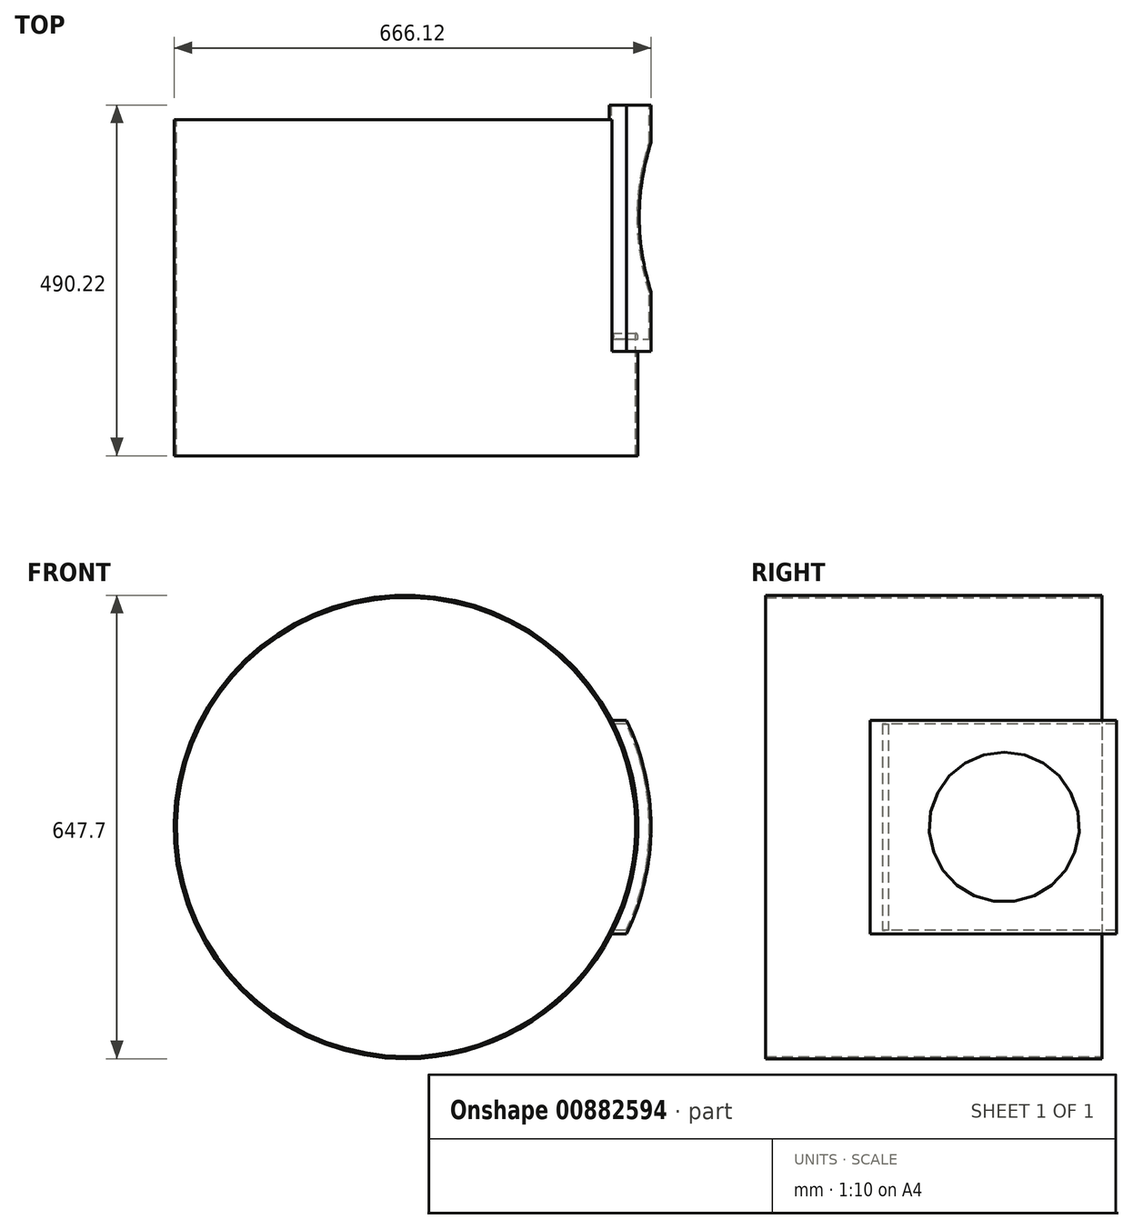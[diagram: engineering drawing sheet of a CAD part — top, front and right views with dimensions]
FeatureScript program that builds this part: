
annotation { "Feature Type Name" : "Feature", "Feature Type Description" : "" }
export const myFeature = defineFeature(function(context is Context, id is Id, definition is map)
    precondition{}
    {
        {
            var Q0;
            Q0=qCreatedBy(makeId("Front.planeOp"),FACE);
            var sketch = newSketch(context, id + "F0", { "sketchPlane" : qUnion([Q0])});
            skCircle(sketch, "E0", {"center": v(0, 0) * mm, "radius": 320.68 * mm});
            skCircle(sketch, "E1", {"center": v(0, 0) * mm, "radius": 323.85 * mm});
            skSolve(sketch);
        }
        {
            var Q0;
            Q0 = qSketchRegion(id + "F0", true);
            extrude(context, id + "F1", {"entities" : qUnion([Q0]), "depth" : 469.9 * mm, "offsetDistance" : 25.4 * mm});
        }
        {
            var Q0;
            Q0=qCreatedBy(makeId("Right.planeOp"),FACE);
            var sketch = newSketch(context, id + "F2", { "sketchPlane" : qUnion([Q0])});
            skLineSegment(sketch, "E2", {"start": v(0, 0) * mm, "end": v(-469.9, 0) * mm, "construction": true});
            skLineSegment(sketch, "E3.bottom", {"start": v(0, 149.23) * mm, "end": v(-298.45, 149.23) * mm});
            skLineSegment(sketch, "E3.top", {"start": v(0, -149.22) * mm, "end": v(-298.45, -149.22) * mm});
            skLineSegment(sketch, "E3.left", {"start": v(0, 149.22) * mm, "end": v(0, -149.23) * mm});
            skLineSegment(sketch, "E3.right", {"start": v(-298.45, 149.23) * mm, "end": v(-298.45, -149.22) * mm});
            skPoint(sketch, "E3.middle", {"position": v(-149.23, 0) * mm});
            skSolve(sketch);
        }
        {
            var Q0;
            Q0 = qSketchRegion(id + "F2", true);
            extrude(context, id + "F3", {"entities" : qUnion([Q0]), "operationType" : NewBodyOperationType.REMOVE, "depth" : 595.88 * mm, "offsetDistance" : 25.4 * mm});
        }
        {
            var Q0;
            Q0=qCreatedBy(makeId("Right.planeOp"),FACE);
            var sketch = newSketch(context, id + "F4", { "sketchPlane" : qUnion([Q0])});
            skLineSegment(sketch, "E4", {"start": v(0, 0) * mm, "end": v(-447.9, 0) * mm, "construction": true});
            skPoint(sketch, "E5", {"position": v(-161.92, 0) * mm});
            skLineSegment(sketch, "E6.bottom", {"start": v(0, 149.23) * mm, "end": v(-323.85, 149.22) * mm});
            skLineSegment(sketch, "E6.top", {"start": v(0, -149.22) * mm, "end": v(-323.85, -149.23) * mm});
            skLineSegment(sketch, "E6.right", {"start": v(-323.85, 149.22) * mm, "end": v(-323.85, -149.23) * mm});
            skLineSegment(sketch, "E7.bottom", {"start": v(-17.14, 144.15) * mm, "end": v(-306.71, 144.15) * mm});
            skLineSegment(sketch, "E7.top", {"start": v(-17.14, -144.15) * mm, "end": v(-306.71, -144.15) * mm});
            skLineSegment(sketch, "E7.right", {"start": v(-306.71, 144.15) * mm, "end": v(-306.71, -144.15) * mm});
            skLineSegment(sketch, "E8", {"start": v(-17.14, -144.15) * mm, "end": v(0, -144.15) * mm});
            skLineSegment(sketch, "E9", {"start": v(-17.14, 144.15) * mm, "end": v(0, 144.15) * mm});
            skLineSegment(sketch, "E10", {"start": v(0, -149.22) * mm, "end": v(20.32, -149.22) * mm});
            skLineSegment(sketch, "E11", {"start": v(20.32, -149.22) * mm, "end": v(20.32, -144.14) * mm});
            skLineSegment(sketch, "E12", {"start": v(0, -144.14) * mm, "end": v(20.32, -144.14) * mm});
            skLineSegment(sketch, "E13.MirrorCS", {"start": v(0, 144.14) * mm, "end": v(20.32, 144.14) * mm});
            skLineSegment(sketch, "E14.MirrorCS", {"start": v(0, 149.22) * mm, "end": v(20.32, 149.22) * mm});
            skLineSegment(sketch, "E15.MirrorCS", {"start": v(20.32, 149.22) * mm, "end": v(20.32, 144.14) * mm});
            skSolve(sketch);
        }
        {
            var Q0;
            Q0 = qSketchRegion(id + "F4", true);
            extrude(context, id + "F5", {"entities" : qUnion([Q0]), "operationType" : NewBodyOperationType.ADD, "depth" : 612.14 * mm, "offsetDistance" : 25.4 * mm});
        }
        {
            var Q0;
            Q0=makeQuery(id+"F3.boolean.opBoolean","INTERSECT",EDGE,{"derivedFrom":[makeQuery(id+"F1.opExtrude","SWEPT_FACE",FACE,{"disambiguationData":[OSD([sQuery(id+"F0.wireOp",EDGE,"E1")])]}),makeQuery(id+"F3.opExtrude","SWEPT_FACE",FACE,{"disambiguationData":[OSD([sQuery(id+"F2.wireOp",EDGE,"E3.bottom")])]})]});
            var Q1;
            Q1=makeQuery(id+"F3.boolean.opBoolean","INTERSECT",EDGE,{"derivedFrom":[makeQuery(id+"F1.opExtrude","SWEPT_FACE",FACE,{"disambiguationData":[OSD([sQuery(id+"F0.wireOp",EDGE,"E1")])]}),makeQuery(id+"F3.opExtrude","SWEPT_FACE",FACE,{"disambiguationData":[OSD([sQuery(id+"F2.wireOp",EDGE,"E3.right")])]})]});
            var Q2;
            Q2=makeQuery(id+"F3.boolean.opBoolean","INTERSECT",EDGE,{"derivedFrom":[makeQuery(id+"F1.opExtrude","SWEPT_FACE",FACE,{"disambiguationData":[OSD([sQuery(id+"F0.wireOp",EDGE,"E1")])]}),makeQuery(id+"F3.opExtrude","SWEPT_FACE",FACE,{"disambiguationData":[OSD([sQuery(id+"F2.wireOp",EDGE,"E3.top")])]})]});
            fillet(context, id + "F6", {"entities" : qUnion([Q0, Q1, Q2]), "radius" : 5.08 * mm, "tangentPropagation" : true, "allowEdgeOverflow" : false});
        }
        {
            var Q0;
            Q0=qCreatedBy(makeId("Front.planeOp"),FACE);
            var sketch = newSketch(context, id + "F7", { "sketchPlane" : qUnion([Q0])});
            skCircle(sketch, "E16", {"center": v(0, 0) * mm, "radius": 320.68 * mm});
            skCircle(sketch, "E17", {"center": v(0, 0) * mm, "radius": 339.73 * mm});
            skCircle(sketch, "E18", {"center": v(0, 0) * mm, "radius": 669.26 * mm});
            skSolve(sketch);
        }
        {
            var Q0;
            Q0 = qSketchRegion(id + "F7", true);
            var Q1;
            Q1=makeQuery(id+"F7.imprint","IMPRINT",FACE,{"disambiguationData":[TD([[makeQuery(id+"F7.imprint","IMPRINT",EDGE,{"derivedFrom":sQuery(id+"F7.wireOp",EDGE,"E16")}),1.0]])]});
            extrude(context, id + "F8", {"entities" : qUnion([Q0, Q1]), "operationType" : NewBodyOperationType.REMOVE, "endBound" : BoundingType.SYMMETRIC, "oppositeDirection" : true, "depth" : 1122.68 * mm, "offsetDistance" : 25.4 * mm});
        }
        {
            var Q0;
            Q0=qCreatedBy(makeId("Front.planeOp"),FACE);
            var sketch = newSketch(context, id + "F9", { "sketchPlane" : qUnion([Q0])});
            skArc(sketch, "E19", {"start": v(305.2, -149.23) * mm, "mid": v(339.73, 0) * mm, "end": v(305.2, 149.22) * mm});
            skLineSegment(sketch, "E20", {"start": v(0, 0) * mm, "end": v(0, 149.23) * mm, "construction": true});
            skLineSegment(sketch, "E21", {"start": v(0, 0) * mm, "end": v(501.28, 0) * mm, "construction": true});
            skLineSegment(sketch, "E22", {"start": v(305.2, 149.23) * mm, "end": v(308.02, 149.23) * mm});
            skArc(sketch, "E23", {"start": v(308.02, -149.23) * mm, "mid": v(342.26, 0) * mm, "end": v(308.02, 149.22) * mm});
            skLineSegment(sketch, "E24.MirrorCS", {"start": v(305.2, -149.23) * mm, "end": v(308.02, -149.23) * mm});
            skPoint(sketch, "E25.orphan", {"position": v(0, -149.23) * mm});
            skSolve(sketch);
        }
        {
            var Q0;
            Q0 = qSketchRegion(id + "F9", true);
            var Q1;
            {var subQ1=sQuery(id+"F4.wireOp",EDGE,"E6.right");Q1=makeQuery(id+"F5.boolean.opBoolean","SPLIT",FACE,{"disambiguationData":[TD([makeQuery(id+"F1.opExtrude","SWEPT_FACE",FACE,{"disambiguationData":[OSD([sQuery(id+"F0.wireOp",EDGE,"E1")])]})])],"derivedFrom":makeQuery(id+"F5.opExtrude","SWEPT_FACE",FACE,{"disambiguationData":[OSD([subQ1])]})});}
            extrude(context, id + "F10", {"entities" : qUnion([Q0]), "operationType" : NewBodyOperationType.ADD, "endBound" : BoundingType.UP_TO_SURFACE, "depth" : 298.45 * mm, "endBoundEntityFace" : qUnion([Q1]), "offsetDistance" : 25.4 * mm});
        }
        {
            var Q0;
            Q0=qCreatedBy(makeId("Right.planeOp"),FACE);
            var sketch = newSketch(context, id + "F11", { "sketchPlane" : qUnion([Q0])});
            skCircle(sketch, "E26", {"center": v(-136.53, 0) * mm, "radius": 104.78 * mm});
            skSolve(sketch);
        }
        {
            var Q0;
            Q0 = qSketchRegion(id + "F11", true);
            extrude(context, id + "F12", {"entities" : qUnion([Q0]), "operationType" : NewBodyOperationType.REMOVE, "depth" : 947.42 * mm, "offsetDistance" : 25.4 * mm});
        }
        {
            var Q0;
            Q0 = qSketchRegion(id + "F9", true);
            extrude(context, id + "F13", {"entities" : qUnion([Q0]), "operationType" : NewBodyOperationType.ADD, "oppositeDirection" : true, "depth" : 20.32 * mm, "offsetDistance" : 25.4 * mm});
        }
    });
